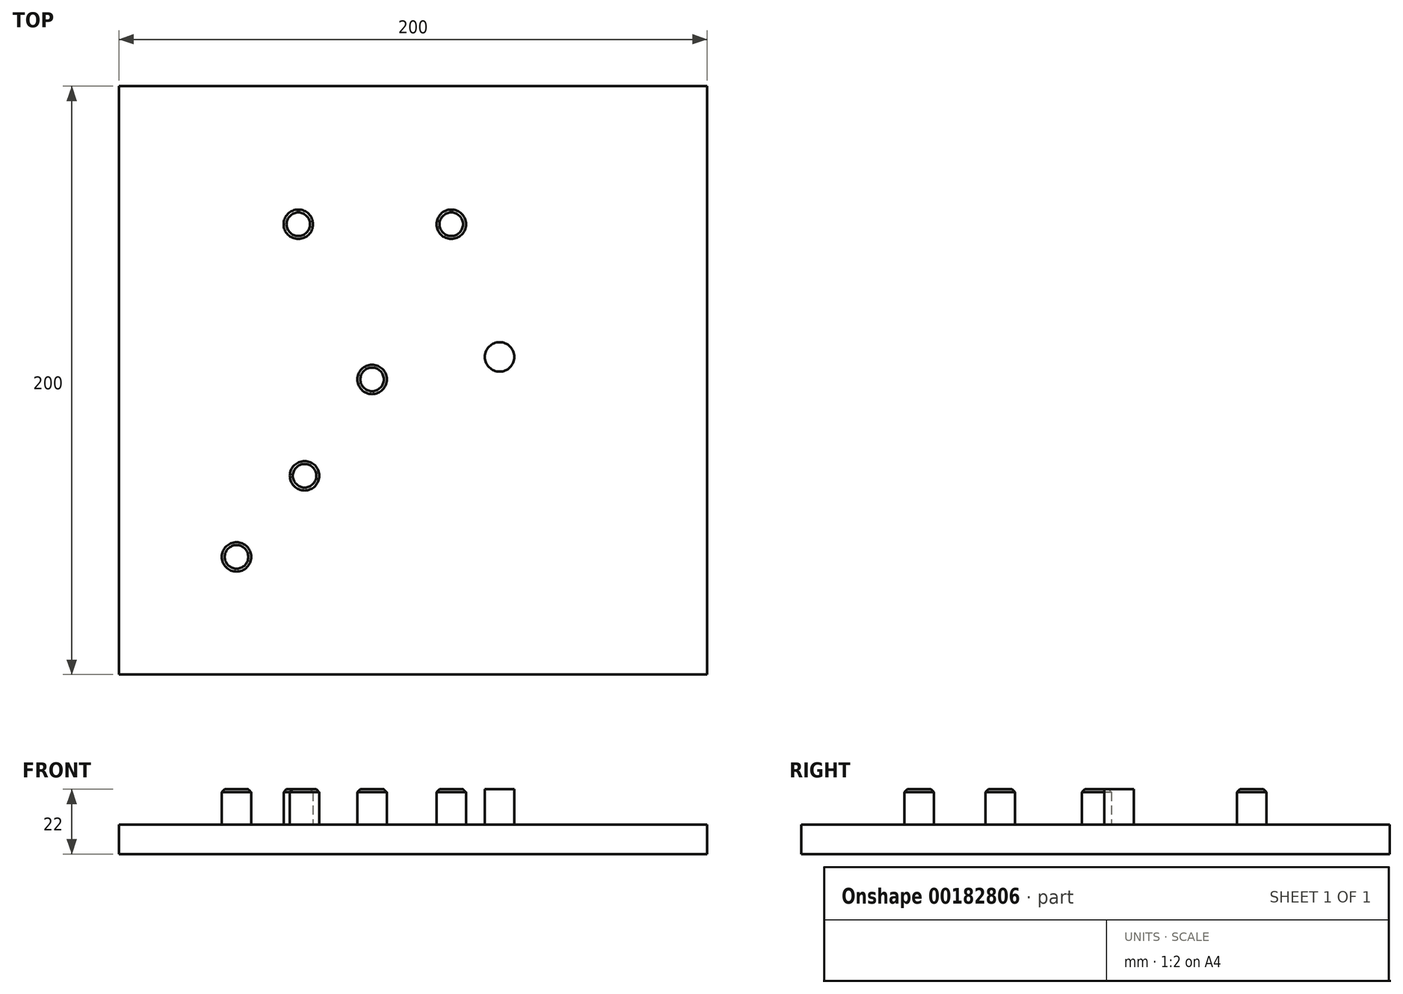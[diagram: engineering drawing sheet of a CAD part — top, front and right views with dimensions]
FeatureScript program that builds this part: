
annotation { "Feature Type Name" : "Feature", "Feature Type Description" : "" }
export const myFeature = defineFeature(function(context is Context, id is Id, definition is map)
    precondition{}
    {
        {
            var Q0;
            Q0=qCreatedBy(makeId("Top.planeOp"),FACE);
            var sketch = newSketch(context, id + "F0", { "sketchPlane" : qUnion([Q0])});
            skLineSegment(sketch, "E0.bottom", {"start": v(100, -100) * mm, "end": v(-100, -100) * mm});
            skLineSegment(sketch, "E0.top", {"start": v(100, 100) * mm, "end": v(-100, 100) * mm});
            skLineSegment(sketch, "E0.left", {"start": v(100, -100) * mm, "end": v(100, 100) * mm});
            skLineSegment(sketch, "E0.right", {"start": v(-100, -100) * mm, "end": v(-100, 100) * mm});
            skPoint(sketch, "E0.middle", {"position": v(0, 0) * mm});
            skSolve(sketch);
        }
        {
            var Q0;
            Q0 = qSketchRegion(id + "F0", true);
            extrude(context, id + "F1", {"entities" : qUnion([Q0]), "depth" : 10 * mm});
        }
        {
            var Q0;
            Q0=makeQuery(id+"F1.opExtrude","CAP_FACE",FACE,{"disambiguationData":[OSD([sQuery(id+"F0.wireOp",EDGE,"E0.bottom"),sQuery(id+"F0.wireOp",EDGE,"E0.top"),sQuery(id+"F0.wireOp",EDGE,"E0.left"),sQuery(id+"F0.wireOp",EDGE,"E0.right")])],"isStart":false});
            var sketch = newSketch(context, id + "F2", { "sketchPlane" : qUnion([Q0])});
            skCircle(sketch, "E1", {"center": v(-60, -60) * mm, "radius": 5 * mm});
            skCircle(sketch, "E2", {"center": v(-36.86, -32.42) * mm, "radius": 5 * mm});
            skCircle(sketch, "E3", {"center": v(-13.92, 0.34) * mm, "radius": 5 * mm});
            skCircle(sketch, "E4", {"center": v(29.41, 7.98) * mm, "radius": 5 * mm});
            skCircle(sketch, "E5", {"center": v(13, 53.09) * mm, "radius": 5 * mm});
            skCircle(sketch, "E6", {"center": v(-39, 53.09) * mm, "radius": 5 * mm});
            skLineSegment(sketch, "E7", {"start": v(-60, -60) * mm, "end": v(-36.86, -32.42) * mm});
            skLineSegment(sketch, "E8", {"start": v(-36.86, -32.42) * mm, "end": v(-13.92, 0.34) * mm});
            skLineSegment(sketch, "E9", {"start": v(-13.92, 0.34) * mm, "end": v(29.41, 7.98) * mm});
            skLineSegment(sketch, "E10", {"start": v(29.41, 7.98) * mm, "end": v(13, 53.09) * mm});
            skLineSegment(sketch, "E11", {"start": v(-39, 53.09) * mm, "end": v(13, 53.09) * mm});
            skLineSegment(sketch, "E12", {"start": v(-60, -60) * mm, "end": v(-27.4, -60) * mm});
            skSolve(sketch);
        }
        {
            var Q0;
            Q0 = qSketchRegion(id + "F2", true);
            extrude(context, id + "F3", {"entities" : qUnion([Q0]), "operationType" : NewBodyOperationType.ADD, "depth" : 12 * mm});
        }
        {
            var Q0;
            Q0=makeQuery(id+"F3.opExtrude","CAP_EDGE",EDGE,{"disambiguationData":[OSD([sQuery(id+"F2.wireOp",EDGE,"E1")])],"isStart":false});
            var Q1;
            Q1=makeQuery(id+"F3.opExtrude","CAP_EDGE",EDGE,{"disambiguationData":[OSD([sQuery(id+"F2.wireOp",EDGE,"E2")])],"isStart":false});
            var Q2;
            Q2=makeQuery(id+"F3.opExtrude","CAP_EDGE",EDGE,{"disambiguationData":[OSD([sQuery(id+"F2.wireOp",EDGE,"E3")])],"isStart":false});
            var Q3;
            Q3=makeQuery(id+"F3.opExtrude","CAP_EDGE",EDGE,{"disambiguationData":[OSD([sQuery(id+"F2.wireOp",EDGE,"E5")])],"isStart":false});
            var Q4;
            Q4=makeQuery(id+"F3.opExtrude","CAP_EDGE",EDGE,{"disambiguationData":[OSD([sQuery(id+"F2.wireOp",EDGE,"E6")])],"isStart":false});
            chamfer(context, id + "F4", {"entities" : qUnion([Q0, Q1, Q2, Q3, Q4]), "width" : 1 * mm, "tangentPropagation" : true});
        }
    });
